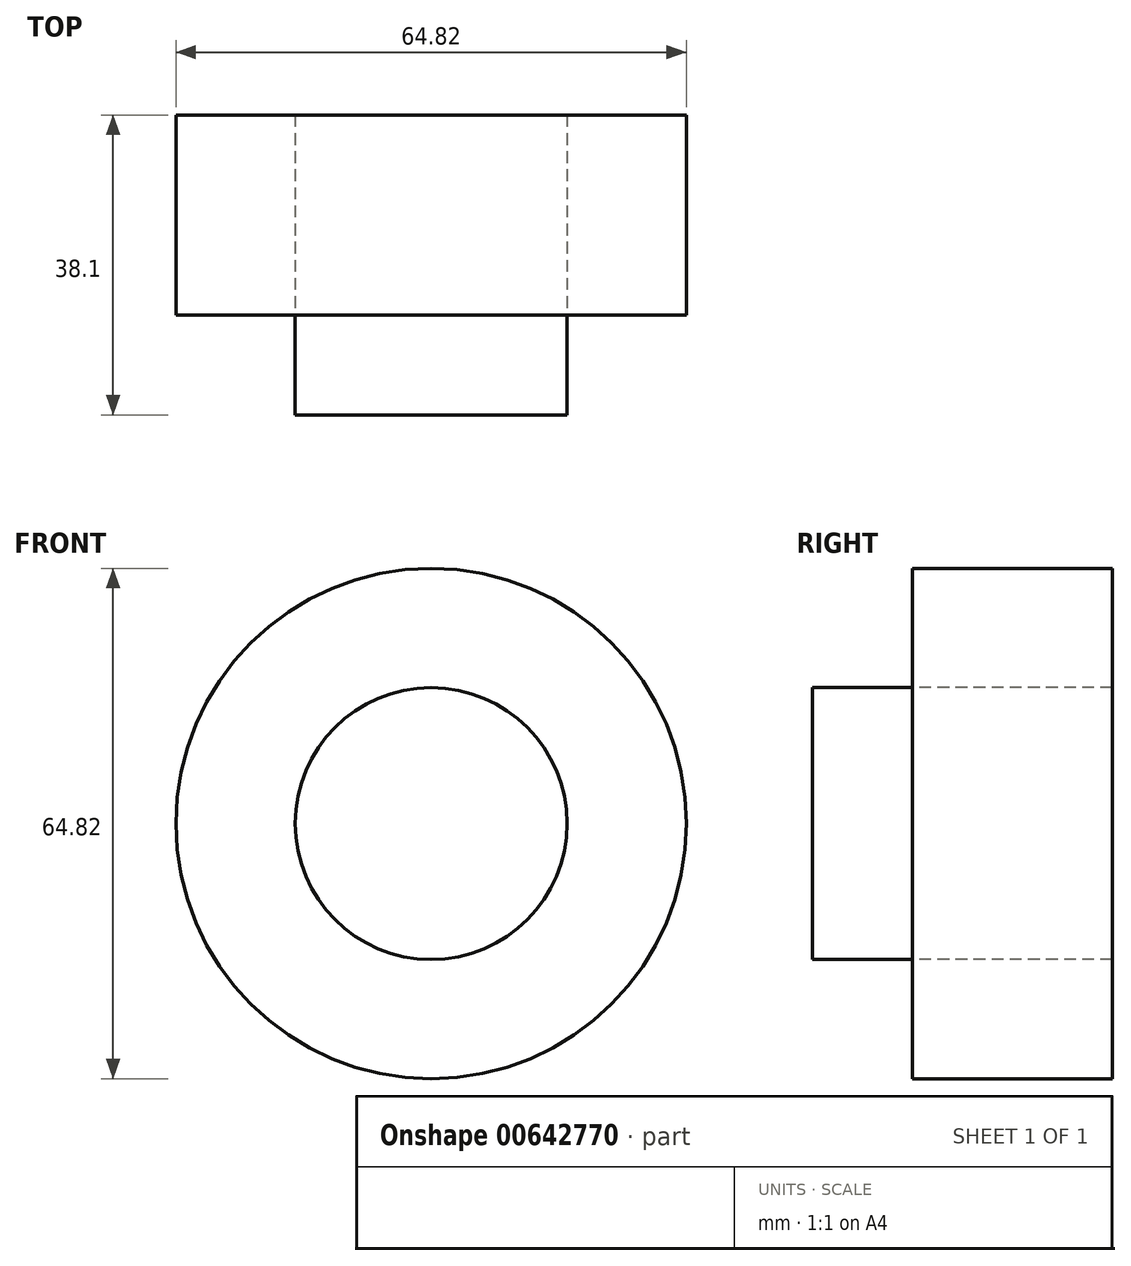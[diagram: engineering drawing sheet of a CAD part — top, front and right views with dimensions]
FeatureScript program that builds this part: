
annotation { "Feature Type Name" : "Feature", "Feature Type Description" : "" }
export const myFeature = defineFeature(function(context is Context, id is Id, definition is map)
    precondition{}
    {
        {
            var Q0;
            Q0=qCreatedBy(makeId("Front.planeOp"),FACE);
            var sketch = newSketch(context, id + "F0", { "sketchPlane" : qUnion([Q0])});
            skCircle(sketch, "E0", {"center": v(0, 0) * mm, "radius": 32.41 * mm});
            skSolve(sketch);
        }
        {
            var Q0;
            Q0=sQuery(id+"F0.wireOp",EDGE,"E0");
            extrude(context, id + "F1", {"bodyType" : ToolBodyType.SURFACE, "surfaceEntities" : qUnion([Q0]), "depth" : 25.4 * mm, "offsetDistance" : 25.4 * mm});
        }
        {
            var Q0;
            Q0=qCreatedBy(makeId("Front.planeOp"),FACE);
            var sketch = newSketch(context, id + "F2", { "sketchPlane" : qUnion([Q0])});
            skCircle(sketch, "E1", {"center": v(0, 0) * mm, "radius": 17.27 * mm});
            skSolve(sketch);
        }
        {
            var Q0;
            Q0=sQuery(id+"F2.wireOp",EDGE,"E1");
            extrude(context, id + "F3", {"bodyType" : ToolBodyType.SURFACE, "surfaceEntities" : qUnion([Q0]), "depth" : 38.1 * mm, "offsetDistance" : 25.4 * mm});
        }
    });
